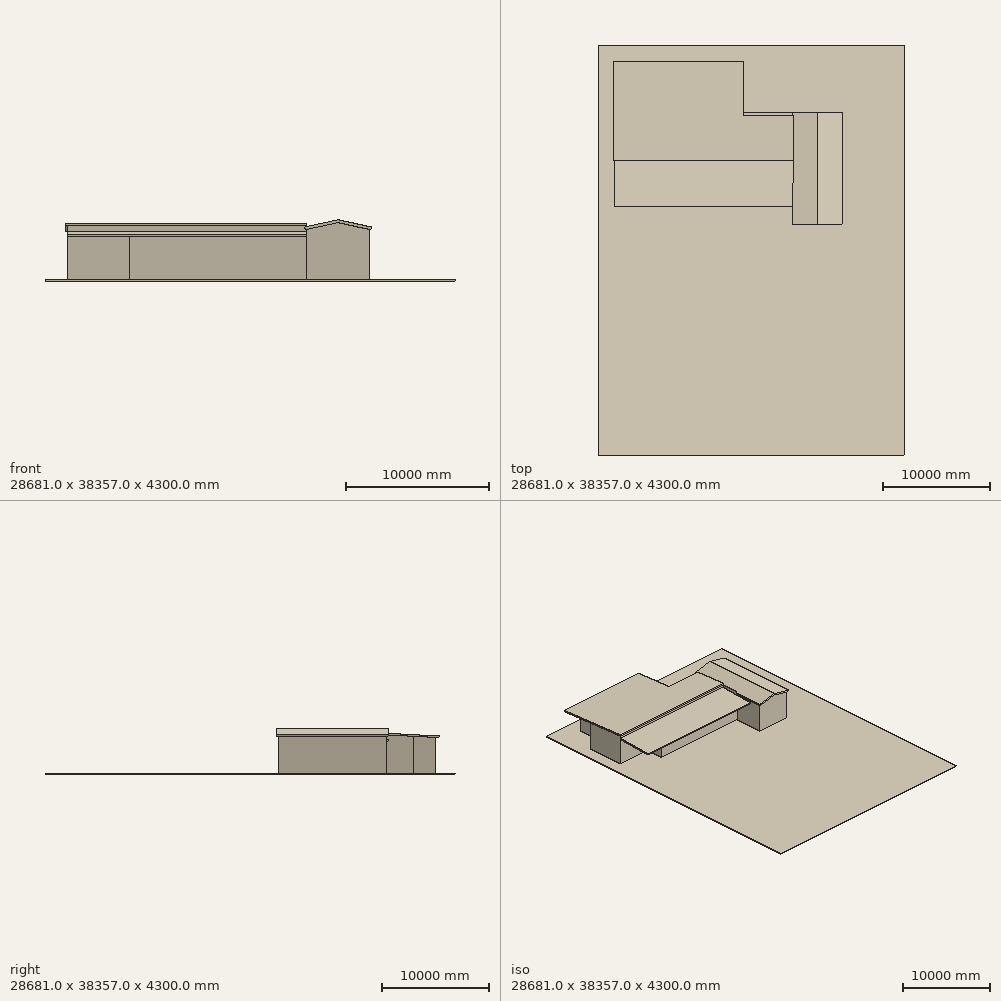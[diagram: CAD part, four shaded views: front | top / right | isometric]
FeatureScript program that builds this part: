
annotation { "Feature Type Name" : "Feature", "Feature Type Description" : "" }
export const myFeature = defineFeature(function(context is Context, id is Id, definition is map)
    precondition{}
    {
        {
            var Q0;
            Q0=qCreatedBy(makeId("Top.planeOp"),FACE);
            var sketch = newSketch(context, id + "F0", { "sketchPlane" : qUnion([Q0])});
            skLineSegment(sketch, "E0.bottom", {"start": v(0, 0) * mm, "end": v(-28681, 0) * mm});
            skLineSegment(sketch, "E0.top", {"start": v(0, -38357) * mm, "end": v(-28681, -38357) * mm});
            skLineSegment(sketch, "E0.left", {"start": v(0, 0) * mm, "end": v(0, -38357) * mm});
            skLineSegment(sketch, "E0.right", {"start": v(-28681, 0) * mm, "end": v(-28681, -38357) * mm});
            skSolve(sketch);
        }
        {
            var Q0;
            Q0=makeQuery(id+"F0.imprint","IMPRINT",FACE,{"disambiguationData":[TD([[makeQuery(id+"F0.imprint","IMPRINT",EDGE,{"derivedFrom":sQuery(id+"F0.wireOp",EDGE,"E0.bottom")}),1.0]])]});
            extrude(context, id + "F1", {"entities" : qUnion([Q0]), "oppositeDirection" : true, "depth" : 100 * mm, "offsetDistance" : 25 * mm});
        }
        {
            var Q0;
            Q0=makeQuery(id+"F1.opExtrude","CAP_FACE",FACE,{"disambiguationData":[OSD([sQuery(id+"F0.wireOp",EDGE,"E0.bottom"),sQuery(id+"F0.wireOp",EDGE,"E0.top"),sQuery(id+"F0.wireOp",EDGE,"E0.left"),sQuery(id+"F0.wireOp",EDGE,"E0.right")])],"isStart":true});
            var sketch = newSketch(context, id + "F2", { "sketchPlane" : qUnion([Q0])});
            skLineSegment(sketch, "E1.bottom", {"start": v(-10396, -6495) * mm, "end": v(-6011, -6495) * mm});
            skLineSegment(sketch, "E1.top", {"start": v(-10396, -16565) * mm, "end": v(-6011, -16565) * mm});
            skLineSegment(sketch, "E1.left", {"start": v(-10396, -6495) * mm, "end": v(-10396, -16565) * mm});
            skLineSegment(sketch, "E1.right", {"start": v(-6011, -6495) * mm, "end": v(-6011, -16565) * mm});
            skSolve(sketch);
        }
        {
            var Q0;
            Q0=makeQuery(id+"F2.imprint","IMPRINT",FACE,{"disambiguationData":[TD([[makeQuery(id+"F2.imprint","IMPRINT",EDGE,{"derivedFrom":sQuery(id+"F2.wireOp",EDGE,"E1.bottom")}),-1.0]])]});
            extrude(context, id + "F3", {"entities" : qUnion([Q0]), "operationType" : NewBodyOperationType.ADD, "depth" : 4500 * mm, "offsetDistance" : 25 * mm});
        }
        {
            var Q0;
            Q0=makeQuery(id+"F1.opExtrude","CAP_FACE",FACE,{"disambiguationData":[OSD([sQuery(id+"F0.wireOp",EDGE,"E0.bottom"),sQuery(id+"F0.wireOp",EDGE,"E0.top"),sQuery(id+"F0.wireOp",EDGE,"E0.left"),sQuery(id+"F0.wireOp",EDGE,"E0.right")])],"isStart":true});
            var sketch = newSketch(context, id + "F4", { "sketchPlane" : qUnion([Q0])});
            skLineSegment(sketch, "E2", {"start": v(-10396, -6525) * mm, "end": v(-15366, -6525) * mm});
            skLineSegment(sketch, "E3", {"start": v(-15366, -6525) * mm, "end": v(-15366, -3895) * mm});
            skLineSegment(sketch, "E4", {"start": v(-15366, -3895) * mm, "end": v(-18866, -3895) * mm});
            skLineSegment(sketch, "E5", {"start": v(-18866, -3895) * mm, "end": v(-18866, -1895) * mm});
            skLineSegment(sketch, "E6", {"start": v(-18866, -1895) * mm, "end": v(-25026, -1895) * mm});
            skLineSegment(sketch, "E7", {"start": v(-25026, -1895) * mm, "end": v(-25026, -5595) * mm});
            skLineSegment(sketch, "E8", {"start": v(-25026, -5595) * mm, "end": v(-27126, -5595) * mm});
            skLineSegment(sketch, "E9", {"start": v(-27126, -5595) * mm, "end": v(-27126, -10575) * mm});
            skLineSegment(sketch, "E10", {"start": v(-27126, -10575) * mm, "end": v(-22776, -10575) * mm});
            skLineSegment(sketch, "E11", {"start": v(-22776, -10575) * mm, "end": v(-22776, -12875) * mm});
            skLineSegment(sketch, "E12", {"start": v(-22776, -12875) * mm, "end": v(-10396, -12875) * mm});
            skSolve(sketch);
        }
        {
            var Q0;
            {var subQ0=sQuery(id+"F4.wireOp",EDGE,"E2");Q0=makeQuery(id+"F4.imprint","IMPRINT",FACE,{"disambiguationData":[TD([[makeQuery(id+"F4.imprint","IMPRINT",EDGE,{"derivedFrom":subQ0}),1.0]])]});}
            extrude(context, id + "F5", {"entities" : qUnion([Q0]), "operationType" : NewBodyOperationType.ADD, "depth" : 4000 * mm, "offsetDistance" : 25 * mm});
        }
        {
            var Q0;
            Q0=makeQuery(id+"F3.opExtrude","SWEPT_FACE",FACE,{"disambiguationData":[OSD([sQuery(id+"F2.wireOp",EDGE,"E1.top")])]});
            var sketch = newSketch(context, id + "F6", { "sketchPlane" : qUnion([Q0])});
            skLineSegment(sketch, "E13", {"start": v(-10396, 3720) * mm, "end": v(-8203.5, 4200) * mm});
            skPoint(sketch, "E13.endSnap0", {"position": v(-8203.5, 4500) * mm});
            skLineSegment(sketch, "E14", {"start": v(-8203.5, 4200) * mm, "end": v(-6011, 3720) * mm});
            skSolve(sketch);
        }
        {
            var Q0;
            {var subQ3=sQuery(id+"F6.wireOp",EDGE,"E13");Q0=makeQuery(id+"F6.imprint","IMPRINT",FACE,{"disambiguationData":[TD([[makeQuery(id+"F6.imprint","IMPRINT",EDGE,{"derivedFrom":subQ3}),1.0]])]});}
            extrude(context, id + "F7", {"entities" : qUnion([Q0]), "operationType" : NewBodyOperationType.REMOVE, "endBound" : BoundingType.UP_TO_NEXT, "oppositeDirection" : true, "depth" : 25 * mm, "offsetDistance" : 25 * mm});
        }
        {
            var Q0;
            Q0=makeQuery(id+"F3.opExtrude","SWEPT_FACE",FACE,{"disambiguationData":[OSD([sQuery(id+"F2.wireOp",EDGE,"E1.top")])]});
            extrude(context, id + "F8", {"entities" : qUnion([Q0]), "operationType" : NewBodyOperationType.ADD, "depth" : 25 * mm, "offsetDistance" : 25 * mm});
        }
        {
            var Q0;
            Q0=makeQuery(id+"F8.opExtrude","CAP_FACE",FACE,{"disambiguationData":[OSD([sQuery(id+"F2.wireOp",EDGE,"E1.top")])],"isStart":false});
            var sketch = newSketch(context, id + "F9", { "sketchPlane" : qUnion([Q0])});
            skLineSegment(sketch, "E15", {"start": v(-8203.5, 4200) * mm, "end": v(-10547.97, 3686.73) * mm});
            skLineSegment(sketch, "E16", {"start": v(-10547.97, 3686.73) * mm, "end": v(-10505.2, 3491.36) * mm});
            skLineSegment(sketch, "E17", {"start": v(-10505.2, 3491.36) * mm, "end": v(-8203.5, 3995.26) * mm});
            skLineSegment(sketch, "E18", {"start": v(-8203.5, 3995.26) * mm, "end": v(-5901.8, 3491.36) * mm});
            skLineSegment(sketch, "E19", {"start": v(-5901.8, 3491.36) * mm, "end": v(-5859.03, 3686.73) * mm});
            skLineSegment(sketch, "E20", {"start": v(-5859.03, 3686.73) * mm, "end": v(-8203.5, 4200) * mm});
            skSolve(sketch);
        }
        {
            var Q0;
            {var subQ0=sQuery(id+"F9.wireOp",EDGE,"E20");var subQ1=sQuery(id+"F9.wireOp",EDGE,"E15");var subQ2=makeQuery(id+"F9.imprint","INTERSECT",VERTEX,{"derivedFrom":[subQ1,subQ0]});Q0=makeQuery(id+"F9.imprint","IMPRINT",FACE,{"disambiguationData":[TD([[makeQuery(id+"F9.imprint","IMPRINT",EDGE,{"disambiguationData":[TD([[subQ2,1.0]])],"derivedFrom":subQ1}),-1.0]])]});}
            var Q1;
            {var subQ3=sQuery(id+"F9.wireOp",EDGE,"E16");Q1=makeQuery(id+"F9.imprint","IMPRINT",FACE,{"disambiguationData":[TD([[makeQuery(id+"F9.imprint","IMPRINT",EDGE,{"derivedFrom":subQ3}),1.0]])]});}
            var Q2;
            {var subQ0=sQuery(id+"F9.wireOp",EDGE,"E19");Q2=makeQuery(id+"F9.imprint","IMPRINT",FACE,{"disambiguationData":[TD([[makeQuery(id+"F9.imprint","IMPRINT",EDGE,{"derivedFrom":subQ0}),1.0]])]});}
            extrude(context, id + "F10", {"entities" : qUnion([Q0, Q1, Q2]), "operationType" : NewBodyOperationType.ADD, "oppositeDirection" : true, "depth" : 10300 * mm, "offsetDistance" : 25 * mm, "hasSecondDirection" : true, "secondDirectionOppositeDirection" : false, "secondDirectionDepth" : 200 * mm});
        }
        {
            var Q0;
            Q0=makeQuery(id+"F5.opExtrude","SWEPT_FACE",FACE,{"disambiguationData":[OSD([sQuery(id+"F4.wireOp",EDGE,"E9")])]});
            var sketch = newSketch(context, id + "F11", { "sketchPlane" : qUnion([Q0])});
            skLineSegment(sketch, "E21", {"start": v(1495, 3500) * mm, "end": v(10725, 3970) * mm});
            skLineSegment(sketch, "E22", {"start": v(10725, 3970) * mm, "end": v(10725, 3819.8) * mm});
            skLineSegment(sketch, "E23", {"start": v(10725, 3819.8) * mm, "end": v(1502.63, 3350.2) * mm});
            skLineSegment(sketch, "E24", {"start": v(1502.63, 3350.2) * mm, "end": v(1495, 3500) * mm});
            skSolve(sketch);
        }
        {
            var Q0;
            {var subQ0=sQuery(id+"F11.wireOp",EDGE,"E24");Q0=makeQuery(id+"F11.imprint","IMPRINT",FACE,{"disambiguationData":[TD([[makeQuery(id+"F11.imprint","IMPRINT",EDGE,{"derivedFrom":subQ0}),-1.0]])]});}
            var Q1;
            {var subQ0=sQuery(id+"F11.wireOp",EDGE,"E21");var subQ1=sQuery(id+"F4.wireOp",EDGE,"E9");var subQ2=makeQuery(id+"F5.opExtrude","SWEPT_EDGE",EDGE,{"disambiguationData":[OSD([sQuery(id+"F4.wireOp",EDGE,"E8"),subQ1])]});var subQ3=makeQuery(id+"F11.imprint","INTERSECT",VERTEX,{"derivedFrom":[subQ2,subQ0]});Q1=makeQuery(id+"F11.imprint","IMPRINT",FACE,{"disambiguationData":[TD([[makeQuery(id+"F11.imprint","IMPRINT",EDGE,{"disambiguationData":[TD([[subQ3,-1.0]])],"derivedFrom":subQ0}),-1.0]])]});}
            var Q2;
            {var subQ0=sQuery(id+"F11.wireOp",EDGE,"E22");Q2=makeQuery(id+"F11.imprint","IMPRINT",FACE,{"disambiguationData":[TD([[makeQuery(id+"F11.imprint","IMPRINT",EDGE,{"derivedFrom":subQ0}),-1.0]])]});}
            var Q3;
            {var subQ0=sQuery(id+"F6.wireOp",EDGE,"E13");Q3=makeQuery(id+"F10.boolean.opBoolean","MERGE",FACE,{"derivedFrom":[makeQuery(id+"F8.boolean.opBoolean","MERGE",FACE,{"derivedFrom":[makeQuery(id+"F7.boolean.opBoolean","COPY",FACE,{"derivedFrom":makeQuery(id+"F7.opExtrude","SWEPT_FACE",FACE,{"disambiguationData":[OSD([subQ0])]})}),makeQuery(id+"F8.opExtrude","SWEPT_FACE",FACE,{"disambiguationData":[OSD([subQ0])]})]}),makeQuery(id+"F10.opExtrude","SWEPT_FACE",FACE,{"disambiguationData":[OSD([sQuery(id+"F9.wireOp",EDGE,"E15")])]})]});}
            extrude(context, id + "F12", {"entities" : qUnion([Q0, Q1, Q2]), "operationType" : NewBodyOperationType.ADD, "oppositeDirection" : true, "depth" : 12000 * mm, "endBoundEntityFace" : qUnion([Q3]), "offsetDistance" : 25 * mm, "hasSecondDirection" : true, "secondDirectionOppositeDirection" : false, "secondDirectionDepth" : 150 * mm});
        }
        {
            var Q0;
            {var subQ1=sQuery(id+"F4.wireOp",EDGE,"E7");Q0=makeQuery(id+"F12.boolean.opBoolean","SPLIT",FACE,{"disambiguationData":[TD([makeQuery(id+"F12.opExtrude","SWEPT_FACE",FACE,{"disambiguationData":[OSD([sQuery(id+"F11.wireOp",EDGE,"E21")])]})])],"derivedFrom":makeQuery(id+"F5.opExtrude","SWEPT_FACE",FACE,{"disambiguationData":[OSD([subQ1])]})});}
            extrude(context, id + "F13", {"entities" : qUnion([Q0]), "operationType" : NewBodyOperationType.REMOVE, "endBound" : BoundingType.UP_TO_NEXT, "oppositeDirection" : true, "depth" : 25 * mm, "offsetDistance" : 25 * mm});
        }
        {
            var Q0;
            {var subQ1=sQuery(id+"F4.wireOp",EDGE,"E9");Q0=makeQuery(id+"F12.boolean.opBoolean","SPLIT",FACE,{"disambiguationData":[TD([makeQuery(id+"F12.opExtrude","SWEPT_FACE",FACE,{"disambiguationData":[OSD([sQuery(id+"F11.wireOp",EDGE,"E21")])]})])],"derivedFrom":makeQuery(id+"F5.opExtrude","SWEPT_FACE",FACE,{"disambiguationData":[OSD([subQ1])]})});}
            var Q1;
            Q1=makeQuery(id+"F7.boolean.opBoolean","COPY",FACE,{"derivedFrom":makeQuery(id+"F7.opExtrude","SWEPT_FACE",FACE,{"disambiguationData":[OSD([sQuery(id+"F2.wireOp",EDGE,"E1.top"),sQuery(id+"F2.wireOp",EDGE,"E1.left")])]})});
            extrude(context, id + "F14", {"entities" : qUnion([Q0]), "operationType" : NewBodyOperationType.REMOVE, "endBound" : BoundingType.UP_TO_SURFACE, "oppositeDirection" : true, "depth" : 25 * mm, "endBoundEntityFace" : qUnion([Q1]), "offsetDistance" : 25 * mm});
        }
        {
            var Q0;
            Q0=makeQuery(id+"F12.boolean.opBoolean","SPLIT",FACE,{"disambiguationData":[TD([makeQuery(id+"F12.opExtrude","SWEPT_FACE",FACE,{"disambiguationData":[OSD([sQuery(id+"F11.wireOp",EDGE,"E23")])]})])],"derivedFrom":makeQuery(id+"F5.opExtrude","SWEPT_FACE",FACE,{"disambiguationData":[OSD([sQuery(id+"F4.wireOp",EDGE,"E9")])]})});
            var sketch = newSketch(context, id + "F15", { "sketchPlane" : qUnion([Q0])});
            skLineSegment(sketch, "E25", {"start": v(10575, 3400) * mm, "end": v(15075, 3170) * mm});
            skLineSegment(sketch, "E26", {"start": v(15075, 3170) * mm, "end": v(15067.34, 3020.2) * mm});
            skLineSegment(sketch, "E27", {"start": v(15067.34, 3020.2) * mm, "end": v(10575, 3249.8) * mm});
            skLineSegment(sketch, "E28", {"start": v(10575, 3249.8) * mm, "end": v(6298.04, 3020.24) * mm});
            skLineSegment(sketch, "E29", {"start": v(6298.04, 3020.24) * mm, "end": v(6290, 3170) * mm});
            skLineSegment(sketch, "E30", {"start": v(6290, 3170) * mm, "end": v(10575, 3400) * mm});
            skLineSegment(sketch, "E31", {"start": v(6290, 3170) * mm, "end": v(15075, 3170) * mm, "construction": true});
            skLineSegment(sketch, "E32.0.0", {"start": v(10575, 3812.17) * mm, "end": v(5595, 3558.58) * mm});
            skLineSegment(sketch, "E32.0.1", {"start": v(5595, 3558.58) * mm, "end": v(5595, 0) * mm});
            skLineSegment(sketch, "E32.0.2", {"start": v(5595, 0) * mm, "end": v(10575, 0) * mm});
            skLineSegment(sketch, "E32.0.3", {"start": v(10575, 0) * mm, "end": v(10575, 3812.17) * mm});
            skSolve(sketch);
        }
        {
            var Q0;
            {var subQ0=sQuery(id+"F15.wireOp",EDGE,"E28");Q0=makeQuery(id+"F15.imprint","IMPRINT",FACE,{"disambiguationData":[TD([[makeQuery(id+"F15.imprint","IMPRINT",EDGE,{"derivedFrom":subQ0}),-1.0]])]});}
            var Q1;
            {var subQ0=sQuery(id+"F15.wireOp",EDGE,"E25");Q1=makeQuery(id+"F15.imprint","IMPRINT",FACE,{"disambiguationData":[TD([[makeQuery(id+"F15.imprint","IMPRINT",EDGE,{"derivedFrom":subQ0}),-1.0]])]});}
            var Q2;
            {var subQ0=sQuery(id+"F2.wireOp",EDGE,"E1.left");var subQ1=sQuery(id+"F2.wireOp",EDGE,"E1.top");Q2=makeQuery(id+"F8.boolean.opBoolean","MERGE",FACE,{"derivedFrom":[makeQuery(id+"F7.boolean.opBoolean","SPLIT",FACE,{"disambiguationData":[TD([makeQuery(id+"F3.opExtrude","SWEPT_FACE",FACE,{"disambiguationData":[OSD([subQ1])]})])],"derivedFrom":makeQuery(id+"F3.opExtrude","SWEPT_FACE",FACE,{"disambiguationData":[OSD([subQ0])]})}),makeQuery(id+"F8.opExtrude","SWEPT_FACE",FACE,{"disambiguationData":[OSD([subQ1,subQ0])]})]});}
            extrude(context, id + "F16", {"entities" : qUnion([Q0, Q1]), "operationType" : NewBodyOperationType.ADD, "endBound" : BoundingType.UP_TO_SURFACE, "oppositeDirection" : true, "depth" : 25 * mm, "endBoundEntityFace" : qUnion([Q2]), "offsetDistance" : 25 * mm});
        }
        {
            var Q0;
            {var subQ0=sQuery(id+"F11.wireOp",EDGE,"E21");var subQ5=sQuery(id+"F4.wireOp",EDGE,"E11");Q0=makeQuery(id+"F16.boolean.opBoolean","SPLIT",FACE,{"disambiguationData":[TD([makeQuery(id+"F12.opExtrude","SWEPT_FACE",FACE,{"disambiguationData":[OSD([subQ0])]})])],"derivedFrom":makeQuery(id+"F5.opExtrude","SWEPT_FACE",FACE,{"disambiguationData":[OSD([subQ5])]})});}
            var Q1;
            {var subQ0=sQuery(id+"F2.wireOp",EDGE,"E1.left");var subQ1=sQuery(id+"F2.wireOp",EDGE,"E1.top");Q1=makeQuery(id+"F8.boolean.opBoolean","MERGE",FACE,{"derivedFrom":[makeQuery(id+"F7.boolean.opBoolean","SPLIT",FACE,{"disambiguationData":[TD([makeQuery(id+"F3.opExtrude","SWEPT_FACE",FACE,{"disambiguationData":[OSD([subQ1])]})])],"derivedFrom":makeQuery(id+"F3.opExtrude","SWEPT_FACE",FACE,{"disambiguationData":[OSD([subQ0])]})}),makeQuery(id+"F8.opExtrude","SWEPT_FACE",FACE,{"disambiguationData":[OSD([subQ1,subQ0])]})]});}
            extrude(context, id + "F17", {"entities" : qUnion([Q0]), "operationType" : NewBodyOperationType.REMOVE, "endBound" : BoundingType.UP_TO_SURFACE, "oppositeDirection" : true, "depth" : 25 * mm, "endBoundEntityFace" : qUnion([Q1]), "offsetDistance" : 25 * mm});
        }
    });
